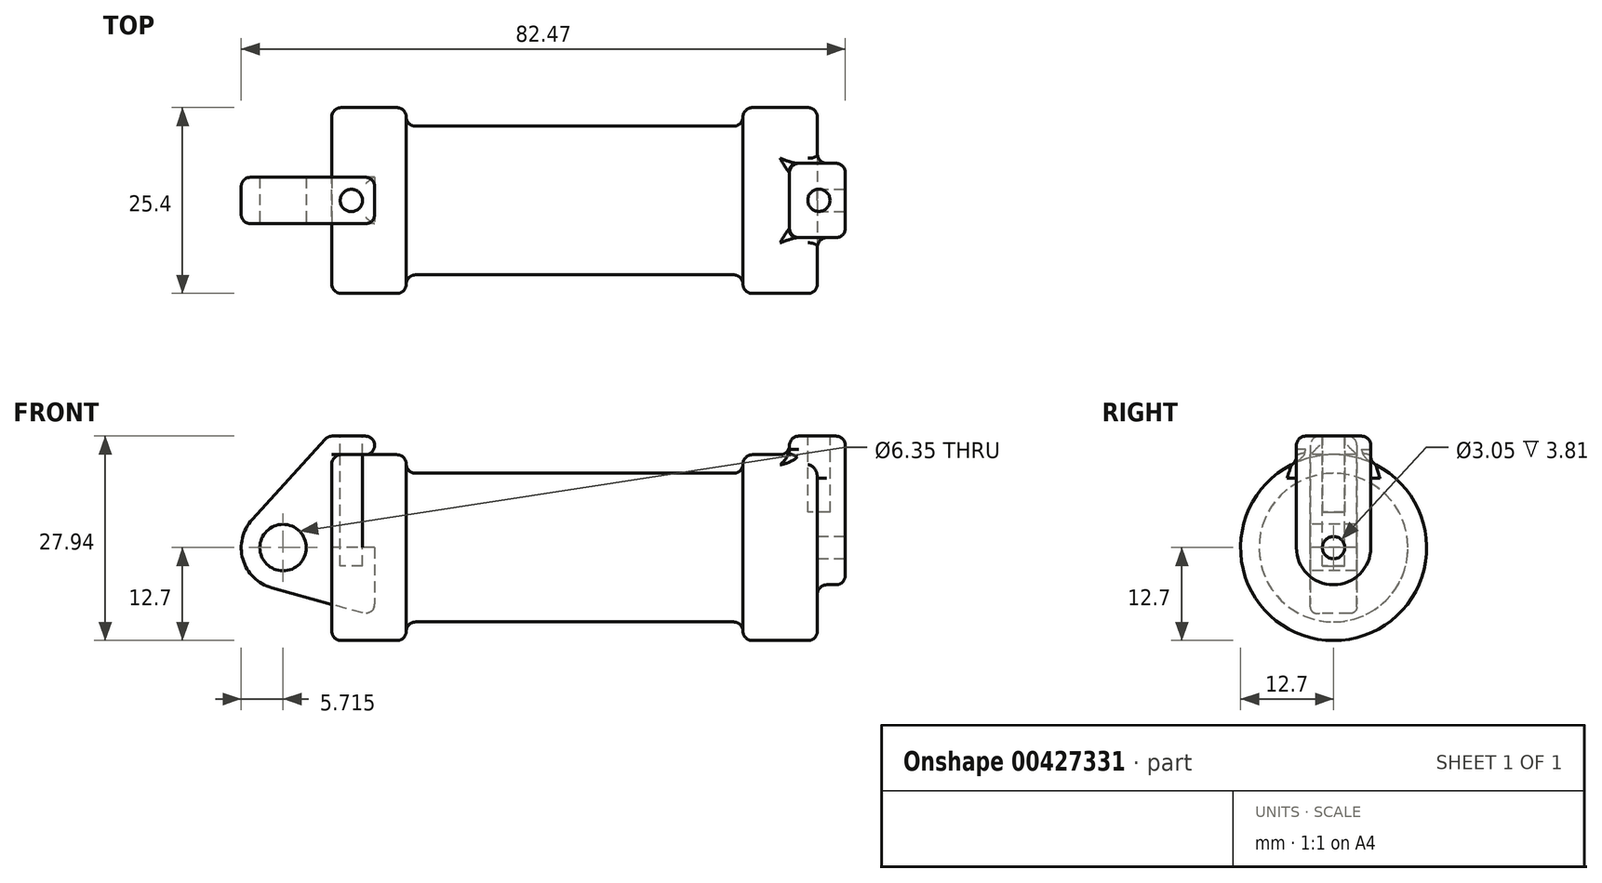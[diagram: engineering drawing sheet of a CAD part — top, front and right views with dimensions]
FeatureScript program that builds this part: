
annotation { "Feature Type Name" : "Feature", "Feature Type Description" : "" }
export const myFeature = defineFeature(function(context is Context, id is Id, definition is map)
    precondition{}
    {
        {
            var Q0;
            Q0=qCreatedBy(makeId("Front.planeOp"),FACE);
            var sketch = newSketch(context, id + "F0", { "sketchPlane" : qUnion([Q0])});
            skLineSegment(sketch, "E0", {"start": v(0, 0) * mm, "end": v(0, 12.7) * mm});
            skLineSegment(sketch, "E1", {"start": v(0, 12.7) * mm, "end": v(10.16, 12.7) * mm});
            skLineSegment(sketch, "E2", {"start": v(10.16, 12.7) * mm, "end": v(10.16, 10.16) * mm});
            skLineSegment(sketch, "E3", {"start": v(10.16, 10.16) * mm, "end": v(56.13, 10.16) * mm});
            skLineSegment(sketch, "E4", {"start": v(56.13, 10.16) * mm, "end": v(56.13, 12.7) * mm});
            skLineSegment(sketch, "E5", {"start": v(56.13, 12.7) * mm, "end": v(66.3, 12.7) * mm});
            skLineSegment(sketch, "E6", {"start": v(66.3, 12.7) * mm, "end": v(66.3, 0) * mm});
            skLineSegment(sketch, "E7", {"start": v(66.3, 0) * mm, "end": v(0, 0) * mm});
            skLineSegment(sketch, "E8", {"start": v(5.84, 15.24) * mm, "end": v(-0.5, 15.24) * mm});
            skLineSegment(sketch, "E9", {"start": v(-0.5, 15.24) * mm, "end": v(-10.88, 3.85) * mm});
            skLineSegment(sketch, "E10", {"start": v(0, 0) * mm, "end": v(-6.65, 0) * mm});
            skCircle(sketch, "E11", {"center": v(-6.65, 0) * mm, "radius": 5.72 * mm});
            skCircle(sketch, "E12", {"center": v(-6.65, 0) * mm, "radius": 3.18 * mm});
            skLineSegment(sketch, "E13", {"start": v(5.84, 15.24) * mm, "end": v(5.84, -9.4) * mm});
            skLineSegment(sketch, "E14", {"start": v(5.84, -9.4) * mm, "end": v(-8.18, -5.5) * mm});
            skSolve(sketch);
        }
        {
            var Q0;
            {var subQ0=sQuery(id+"F0.wireOp",EDGE,"E2");Q0=makeQuery(id+"F0.imprint","IMPRINT",FACE,{"disambiguationData":[TD([[makeQuery(id+"F0.imprint","IMPRINT",EDGE,{"derivedFrom":subQ0}),-1.0]])]});}
            var Q1;
            {var subQ0=sQuery(id+"F0.wireOp",EDGE,"E0");Q1=makeQuery(id+"F0.imprint","IMPRINT",FACE,{"disambiguationData":[TD([[makeQuery(id+"F0.imprint","IMPRINT",EDGE,{"derivedFrom":subQ0}),-1.0]])]});}
            var Q2;
            Q2=sQuery(id+"F0.wireOp",EDGE,"E7");
            revolve(context, id + "F1", {"entities" : qUnion([Q0, Q1]), "axis" : qUnion([Q2]), "revolveType" : RevolveType.FULL});
        }
        {
            var Q0;
            {var subQ5=sQuery(id+"F0.wireOp",EDGE,"E12");Q0=makeQuery(id+"F0.imprint","IMPRINT",FACE,{"disambiguationData":[TD([[makeQuery(id+"F0.imprint","IMPRINT",EDGE,{"derivedFrom":subQ5}),-1.0]])]});}
            var Q1;
            {var subQ1=sQuery(id+"F0.wireOp",EDGE,"E0");Q1=makeQuery(id+"F0.imprint","IMPRINT",FACE,{"disambiguationData":[TD([[makeQuery(id+"F0.imprint","IMPRINT",EDGE,{"derivedFrom":subQ1}),1.0]])]});}
            var Q2;
            {var subQ0=sQuery(id+"F0.wireOp",EDGE,"E14");Q2=makeQuery(id+"F0.imprint","IMPRINT",FACE,{"disambiguationData":[TD([[makeQuery(id+"F0.imprint","IMPRINT",EDGE,{"derivedFrom":subQ0}),-1.0]])]});}
            extrude(context, id + "F2", {"entities" : qUnion([Q0, Q1, Q2]), "endBound" : BoundingType.SYMMETRIC, "oppositeDirection" : true, "depth" : 6.35 * mm});
        }
        {
            var Q0;
            Q0=makeQuery(id+"F1.opRevolve","SWEPT_FACE",FACE,{"disambiguationData":[OSD([sQuery(id+"F0.wireOp",EDGE,"E6")])]});
            var sketch = newSketch(context, id + "F3", { "sketchPlane" : qUnion([Q0])});
            skCircle(sketch, "E15", {"center": v(0, 0) * mm, "radius": 1.52 * mm});
            skCircle(sketch, "E16", {"center": v(0, 0) * mm, "radius": 5.08 * mm});
            skLineSegment(sketch, "E17", {"start": v(-5.08, 0) * mm, "end": v(-5.08, 15.24) * mm});
            skLineSegment(sketch, "E18", {"start": v(-5.08, 15.24) * mm, "end": v(5.08, 15.24) * mm});
            skLineSegment(sketch, "E19", {"start": v(5.08, 15.24) * mm, "end": v(5.08, 0) * mm});
            skSolve(sketch);
        }
        {
            var Q0;
            {var subQ0=sQuery(id+"F3.wireOp",EDGE,"E18");Q0=makeQuery(id+"F3.imprint","IMPRINT",FACE,{"disambiguationData":[TD([[makeQuery(id+"F3.imprint","IMPRINT",EDGE,{"derivedFrom":subQ0}),-1.0]])]});}
            var Q1;
            {var subQ0=sQuery(id+"F3.wireOp",EDGE,"E17");var subQ1=sQuery(id+"F3.wireOp",EDGE,"E16");var subQ2=makeQuery(id+"F3.imprint","INTERSECT",VERTEX,{"derivedFrom":[subQ1,subQ0]});Q1=makeQuery(id+"F3.imprint","IMPRINT",FACE,{"disambiguationData":[TD([[makeQuery(id+"F3.imprint","IMPRINT",EDGE,{"disambiguationData":[TD([[subQ2,1.0]])],"derivedFrom":subQ1}),-1.0]])]});}
            var Q2;
            Q2=makeQuery(id+"F3.imprint","IMPRINT",FACE,{"disambiguationData":[TD([[makeQuery(id+"F3.imprint","IMPRINT",EDGE,{"derivedFrom":sQuery(id+"F3.wireOp",EDGE,"E15")}),-1.0]])]});
            extrude(context, id + "F4", {"entities" : qUnion([Q0, Q1, Q2]), "operationType" : NewBodyOperationType.ADD, "endBound" : BoundingType.SYMMETRIC, "oppositeDirection" : true, "depth" : 7.62 * mm});
        }
        {
            var Q0;
            Q0=makeQuery(id+"F4.opExtrude","SWEPT_FACE",FACE,{"disambiguationData":[OSD([sQuery(id+"F3.wireOp",EDGE,"E18")])]});
            var sketch = newSketch(context, id + "F5", { "sketchPlane" : qUnion([Q0])});
            skCircle(sketch, "E20", {"center": v(66.5, 0.03) * mm, "radius": 1.52 * mm});
            skSolve(sketch);
        }
        {
            var Q0;
            Q0=makeQuery(id+"F5.imprint","IMPRINT",FACE,{"disambiguationData":[TD([[makeQuery(id+"F5.imprint","IMPRINT",EDGE,{"derivedFrom":sQuery(id+"F5.wireOp",EDGE,"E20")}),1.0]])]});
            extrude(context, id + "F6", {"entities" : qUnion([Q0]), "oppositeDirection" : true, "depth" : 10.4 * mm});
        }
        {
            var Q0;
            Q0=makeQuery(id+"F2.opExtrude","SWEPT_FACE",FACE,{"disambiguationData":[OSD([sQuery(id+"F0.wireOp",EDGE,"E8")])]});
            var sketch = newSketch(context, id + "F7", { "sketchPlane" : qUnion([Q0])});
            skCircle(sketch, "E21", {"center": v(2.67, 0) * mm, "radius": 1.52 * mm});
            skPoint(sketch, "E21.centerSnap0", {"position": v(2.67, -3.18) * mm});
            skPoint(sketch, "E21.centerSnap1", {"position": v(-0.5, 0) * mm});
            skSolve(sketch);
        }
        {
            var Q0;
            Q0=makeQuery(id+"F7.imprint","IMPRINT",FACE,{"disambiguationData":[TD([[makeQuery(id+"F7.imprint","IMPRINT",EDGE,{"derivedFrom":sQuery(id+"F7.wireOp",EDGE,"E21")}),1.0]])]});
            extrude(context, id + "F8", {"entities" : qUnion([Q0]), "oppositeDirection" : true, "depth" : 17.78 * mm});
        }
        {
            var Q0;
            Q0=makeQuery(id+"F1.opRevolve","SWEPT_EDGE",EDGE,{"disambiguationData":[OSD([sQuery(id+"F0.wireOp",EDGE,"E1"),sQuery(id+"F0.wireOp",EDGE,"E2")])]});
            var Q1;
            Q1=makeQuery(id+"F1.opRevolve","SWEPT_EDGE",EDGE,{"disambiguationData":[OSD([sQuery(id+"F0.wireOp",EDGE,"E4"),sQuery(id+"F0.wireOp",EDGE,"E5")])]});
            var Q2;
            Q2=makeQuery(id+"F1.opRevolve","SWEPT_EDGE",EDGE,{"disambiguationData":[OSD([sQuery(id+"F0.wireOp",EDGE,"E5"),sQuery(id+"F0.wireOp",EDGE,"E6")])]});
            var Q3;
            Q3=makeQuery(id+"F1.opRevolve","SWEPT_EDGE",EDGE,{"disambiguationData":[OSD([sQuery(id+"F0.wireOp",EDGE,"E0"),sQuery(id+"F0.wireOp",EDGE,"E1")])]});
            var Q4;
            Q4=makeQuery(id+"F1.opRevolve","SWEPT_FACE",FACE,{"disambiguationData":[OSD([sQuery(id+"F0.wireOp",EDGE,"E3")])]});
            var Q5;
            Q5=makeQuery(id+"F1.opRevolve","SWEPT_EDGE",EDGE,{"disambiguationData":[OSD([sQuery(id+"F0.wireOp",EDGE,"E3"),sQuery(id+"F0.wireOp",EDGE,"E4")])]});
            var Q6;
            Q6=makeQuery(id+"F1.opRevolve","SWEPT_FACE",FACE,{"disambiguationData":[OSD([sQuery(id+"F0.wireOp",EDGE,"E5")])]});
            var Q7;
            Q7=makeQuery(id+"F1.opRevolve","SWEPT_FACE",FACE,{"disambiguationData":[OSD([sQuery(id+"F0.wireOp",EDGE,"E1")])]});
            fillet(context, id + "F9", {"entities" : qUnion([Q0, Q1, Q2, Q3, Q4, Q5, Q6, Q7]), "radius" : 1.27 * mm, "tangentPropagation" : true, "allowEdgeOverflow" : false});
        }
        {
            var Q0;
            Q0=makeQuery(id+"F4.opExtrude","SWEPT_FACE",FACE,{"disambiguationData":[OSD([sQuery(id+"F3.wireOp",EDGE,"E18")])]});
            var Q1;
            Q1=makeQuery(id+"F4.opExtrude","SWEPT_FACE",FACE,{"disambiguationData":[OSD([sQuery(id+"F3.wireOp",EDGE,"E17")])]});
            var Q2;
            Q2=makeQuery(id+"F4.opExtrude","SWEPT_FACE",FACE,{"disambiguationData":[OSD([sQuery(id+"F3.wireOp",EDGE,"E19")])]});
            var Q3;
            {var subQ0=makeQuery(id+"F4.opExtrude","SWEPT_FACE",FACE,{"disambiguationData":[OSD([sQuery(id+"F3.wireOp",EDGE,"E16")])]});Q3=makeQuery(id+"F9.opFillet","BLEND_EDGE",EDGE,{"blendedFrom":[makeQuery(id+"F4.boolean.opBoolean","INTERSECT",EDGE,{"derivedFrom":[makeQuery(id+"F1.opRevolve","SWEPT_FACE",FACE,{"disambiguationData":[OSD([sQuery(id+"F0.wireOp",EDGE,"E6")])]}),subQ0]}),subQ0],"blendedInto":[subQ0]});}
            var Q4;
            Q4=makeQuery(id+"F4.opExtrude","SWEPT_FACE",FACE,{"disambiguationData":[OSD([sQuery(id+"F3.wireOp",EDGE,"E16")])]});
            fillet(context, id + "F10", {"entities" : qUnion([Q0, Q1, Q2, Q3, Q4]), "radius" : 1.27 * mm, "tangentPropagation" : true, "allowEdgeOverflow" : false});
        }
        {
            var Q0;
            Q0=makeQuery(id+"F2.opExtrude","SWEPT_FACE",FACE,{"disambiguationData":[OSD([sQuery(id+"F0.wireOp",EDGE,"E9")])]});
            var Q1;
            Q1=makeQuery(id+"F2.opExtrude","SWEPT_FACE",FACE,{"disambiguationData":[OSD([sQuery(id+"F0.wireOp",EDGE,"E14")])]});
            var Q2;
            {var subQ0=sQuery(id+"F0.wireOp",EDGE,"E13");Q2=makeQuery(id+"F2.opExtrude","SWEPT_FACE",FACE,{"disambiguationData":[OSD([subQ0]),TDD([makeQuery(id+"F0.imprint","IMPRINT",EDGE,{"disambiguationData":[TD([[makeQuery(id+"F0.imprint","INTERSECT",VERTEX,{"derivedFrom":[sQuery(id+"F0.wireOp",EDGE,"E8"),subQ0]}),-1.0]])],"derivedFrom":subQ0})])]});}
            var Q3;
            Q3=makeQuery(id+"F2.opExtrude","CAP_EDGE",EDGE,{"disambiguationData":[OSD([sQuery(id+"F0.wireOp",EDGE,"E8")])],"isStart":false});
            var Q4;
            Q4=makeQuery(id+"F2.opExtrude","CAP_EDGE",EDGE,{"disambiguationData":[OSD([sQuery(id+"F0.wireOp",EDGE,"E8")])],"isStart":true});
            var Q5;
            Q5=makeQuery(id+"F2.opExtrude","SWEPT_EDGE",EDGE,{"disambiguationData":[OSD([sQuery(id+"F0.wireOp",EDGE,"E8"),sQuery(id+"F0.wireOp",EDGE,"E9")])]});
            var Q6;
            Q6=makeQuery(id+"F2.opExtrude","SWEPT_EDGE",EDGE,{"disambiguationData":[OSD([sQuery(id+"F0.wireOp",EDGE,"E8"),sQuery(id+"F0.wireOp",EDGE,"E13")])]});
            var Q7;
            Q7=makeQuery(id+"F2.opExtrude","CAP_EDGE",EDGE,{"disambiguationData":[OSD([sQuery(id+"F0.wireOp",EDGE,"E14")])],"isStart":false});
            var Q8;
            Q8=makeQuery(id+"F2.opExtrude","CAP_EDGE",EDGE,{"disambiguationData":[OSD([sQuery(id+"F0.wireOp",EDGE,"E14")])],"isStart":true});
            var Q9;
            Q9=makeQuery(id+"F2.opExtrude","CAP_EDGE",EDGE,{"disambiguationData":[OSD([sQuery(id+"F0.wireOp",EDGE,"E11")])],"isStart":true});
            var Q10;
            Q10=makeQuery(id+"F2.opExtrude","SWEPT_FACE",FACE,{"disambiguationData":[OSD([sQuery(id+"F0.wireOp",EDGE,"E11")])]});
            var Q11;
            Q11=makeQuery(id+"F2.opExtrude","CAP_EDGE",EDGE,{"disambiguationData":[OSD([sQuery(id+"F0.wireOp",EDGE,"E11")])],"isStart":false});
            var Q12;
            Q12=makeQuery(id+"F2.opExtrude","SWEPT_EDGE",EDGE,{"disambiguationData":[OSD([sQuery(id+"F0.wireOp",EDGE,"E1"),sQuery(id+"F0.wireOp",EDGE,"E13")])]});
            fillet(context, id + "F11", {"entities" : qUnion([Q0, Q1, Q2, Q3, Q4, Q5, Q6, Q7, Q8, Q9, Q10, Q11, Q12]), "radius" : 1.27 * mm, "tangentPropagation" : true, "allowEdgeOverflow" : false});
        }
    });
